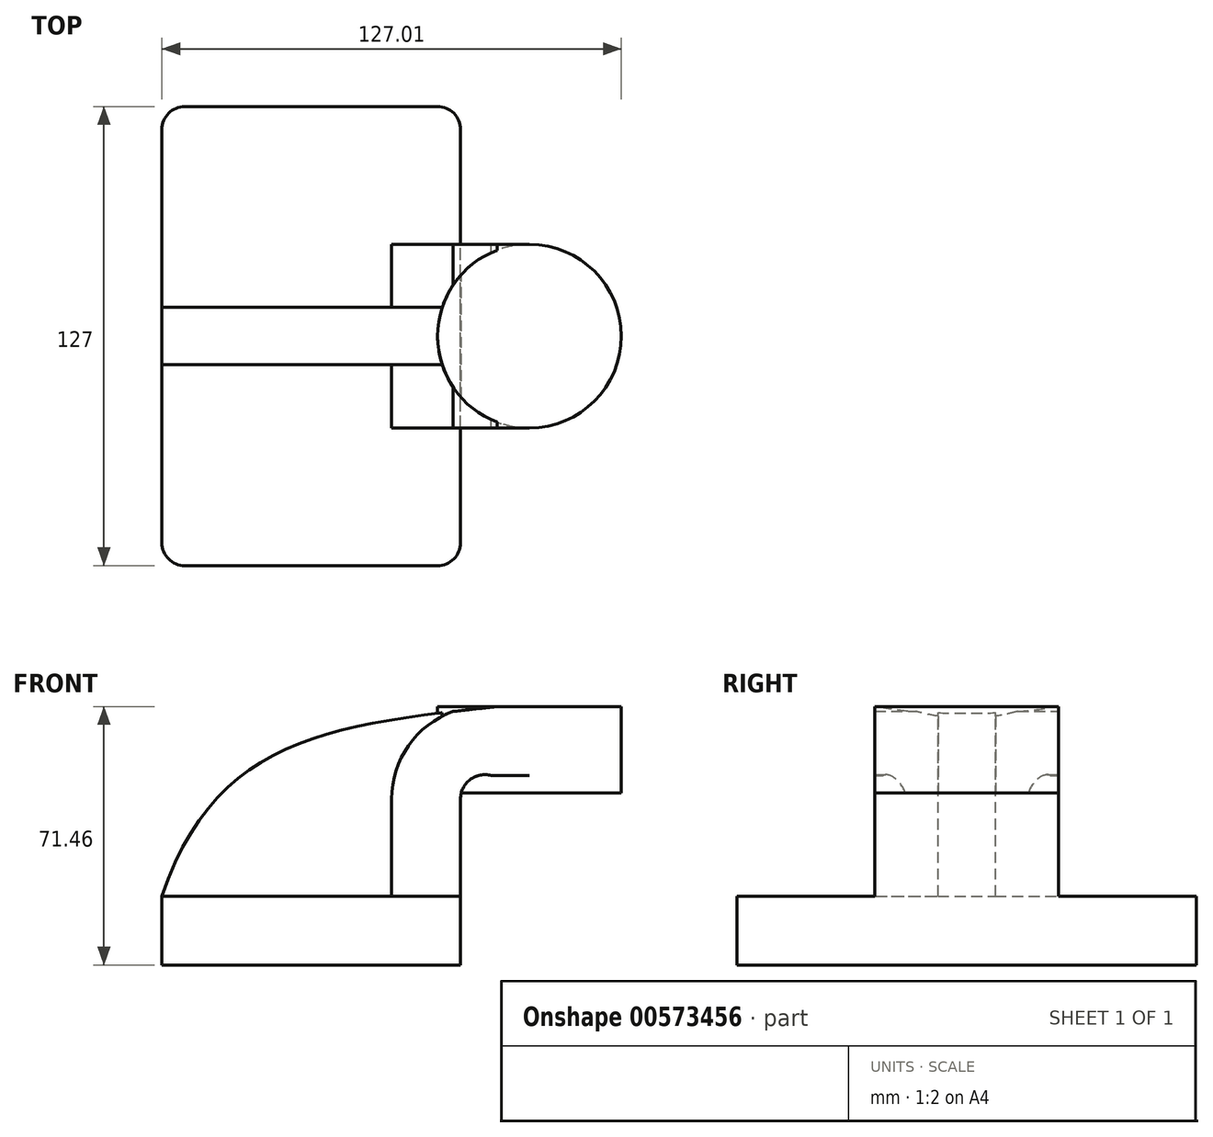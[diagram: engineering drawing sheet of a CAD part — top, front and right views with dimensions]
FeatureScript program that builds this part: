
annotation { "Feature Type Name" : "Feature", "Feature Type Description" : "" }
export const myFeature = defineFeature(function(context is Context, id is Id, definition is map)
    precondition{}
    {
        {
            var Q0;
            Q0=qCreatedBy(makeId("Front.planeOp"),FACE);
            var sketch = newSketch(context, id + "F0", { "sketchPlane" : qUnion([Q0])});
            skLineSegment(sketch, "E0.bottom", {"start": v(-41.28, 9.52) * mm, "end": v(41.28, 9.53) * mm});
            skLineSegment(sketch, "E0.top", {"start": v(-41.28, -9.53) * mm, "end": v(41.28, -9.53) * mm});
            skLineSegment(sketch, "E0.left", {"start": v(-41.28, 9.52) * mm, "end": v(-41.28, -9.53) * mm});
            skLineSegment(sketch, "E0.right", {"start": v(41.28, 9.53) * mm, "end": v(41.28, -9.52) * mm});
            skPoint(sketch, "E0.middle", {"position": v(0, 0) * mm});
            skLineSegment(sketch, "E1.bottom", {"start": v(111.12, 66.68) * mm, "end": v(60.33, 66.68) * mm});
            skLineSegment(sketch, "E1.top", {"start": v(111.12, 38.1) * mm, "end": v(60.33, 38.1) * mm});
            skLineSegment(sketch, "E1.left", {"start": v(111.12, 66.68) * mm, "end": v(111.12, 38.1) * mm});
            skLineSegment(sketch, "E1.right", {"start": v(60.32, 66.68) * mm, "end": v(60.33, 38.1) * mm});
            skPoint(sketch, "E1.middle", {"position": v(85.72, 52.39) * mm});
            skLineSegment(sketch, "E2", {"start": v(41.27, 9.53) * mm, "end": v(41.27, 36.37) * mm});
            skArc(sketch, "E3", {"start": v(41.27, 36.37) * mm, "mid": v(43.9, 41.71) * mm, "end": v(49.74, 42.88) * mm});
            skLineSegment(sketch, "E4", {"start": v(49.74, 42.88) * mm, "end": v(84.42, 42.88) * mm});
            skLineSegment(sketch, "E5.0", {"start": v(51.43, 61.93) * mm, "end": v(85.73, 61.93) * mm});
            skArc(sketch, "E5.1", {"start": v(22.22, 36.37) * mm, "mid": v(31.03, 55.77) * mm, "end": v(51.43, 61.93) * mm});
            skLineSegment(sketch, "E5.2", {"start": v(22.22, 9.53) * mm, "end": v(22.22, 36.37) * mm});
            skLineSegment(sketch, "E6", {"start": v(85.73, 38.1) * mm, "end": v(85.73, 66.68) * mm});
            skFitSpline(sketch, "E7", {"points": [v(-41.28, 9.52) * mm, v(51.43, 61.93) * mm], "startDerivative": vector(44, 129.13) * mm, "endDerivative": vector(143.82, 14.99) * mm});
            skSolve(sketch);
        }
        {
            var Q0;
            Q0=makeQuery(id+"F0.imprint","IMPRINT",FACE,{"disambiguationData":[TD([[makeQuery(id+"F0.imprint","IMPRINT",EDGE,{"derivedFrom":sQuery(id+"F0.wireOp",EDGE,"E0.top")}),1.0]])]});
            extrude(context, id + "F1", {"entities" : qUnion([Q0]), "endBound" : BoundingType.SYMMETRIC, "depth" : 127 * mm, "offsetDistance" : 25.4 * mm});
        }
        {
            var Q0;
            {var subQ1=sQuery(id+"F0.wireOp",EDGE,"E2");Q0=makeQuery(id+"F0.imprint","IMPRINT",FACE,{"disambiguationData":[TD([[makeQuery(id+"F0.imprint","IMPRINT",EDGE,{"derivedFrom":subQ1}),1.0]])]});}
            extrude(context, id + "F2", {"entities" : qUnion([Q0]), "operationType" : NewBodyOperationType.ADD, "endBound" : BoundingType.SYMMETRIC, "depth" : 50.8 * mm, "offsetDistance" : 25.4 * mm});
        }
        {
            var Q0;
            {var subQ3=sQuery(id+"F0.wireOp",EDGE,"E5.2");Q0=makeQuery(id+"F0.imprint","IMPRINT",FACE,{"disambiguationData":[TD([[makeQuery(id+"F0.imprint","IMPRINT",EDGE,{"derivedFrom":subQ3}),1.0]])]});}
            extrude(context, id + "F3", {"entities" : qUnion([Q0]), "operationType" : NewBodyOperationType.ADD, "endBound" : BoundingType.SYMMETRIC, "depth" : 15.88 * mm, "offsetDistance" : 25.4 * mm});
        }
        {
            var Q0;
            {var subQ3=sQuery(id+"F0.wireOp",EDGE,"E1.right");var subQ5=sQuery(id+"F0.wireOp",EDGE,"E1.top");var subQ6=makeQuery(id+"F0.imprint","INTERSECT",VERTEX,{"derivedFrom":[subQ5,subQ3]});Q0=makeQuery(id+"F0.imprint","IMPRINT",FACE,{"disambiguationData":[TD([[makeQuery(id+"F0.imprint","IMPRINT",EDGE,{"disambiguationData":[TD([[subQ6,1.0]])],"derivedFrom":subQ5}),-1.0]])]});}
            var Q1;
            Q1=sQuery(id+"F0.wireOp",EDGE,"E1.right");
            revolve(context, id + "F4", {"operationType" : NewBodyOperationType.ADD, "entities" : qUnion([Q0]), "axis" : qUnion([Q1]), "revolveType" : RevolveType.FULL});
        }
        {
            var Q0;
            Q0=makeQuery(id+"F1.opExtrude","CAP_EDGE",EDGE,{"disambiguationData":[OSD([sQuery(id+"F0.wireOp",EDGE,"E0.right")])],"isStart":false});
            var Q1;
            Q1=makeQuery(id+"F1.opExtrude","CAP_EDGE",EDGE,{"disambiguationData":[OSD([sQuery(id+"F0.wireOp",EDGE,"E0.left")])],"isStart":false});
            var Q2;
            Q2=makeQuery(id+"F1.opExtrude","CAP_EDGE",EDGE,{"disambiguationData":[OSD([sQuery(id+"F0.wireOp",EDGE,"E0.left")])],"isStart":true});
            var Q3;
            Q3=makeQuery(id+"F1.opExtrude","CAP_EDGE",EDGE,{"disambiguationData":[OSD([sQuery(id+"F0.wireOp",EDGE,"E0.right")])],"isStart":true});
            fillet(context, id + "F5", {"entities" : qUnion([Q0, Q1, Q2, Q3]), "radius" : 6.35 * mm, "tangentPropagation" : true, "allowEdgeOverflow" : false});
        }
    });
